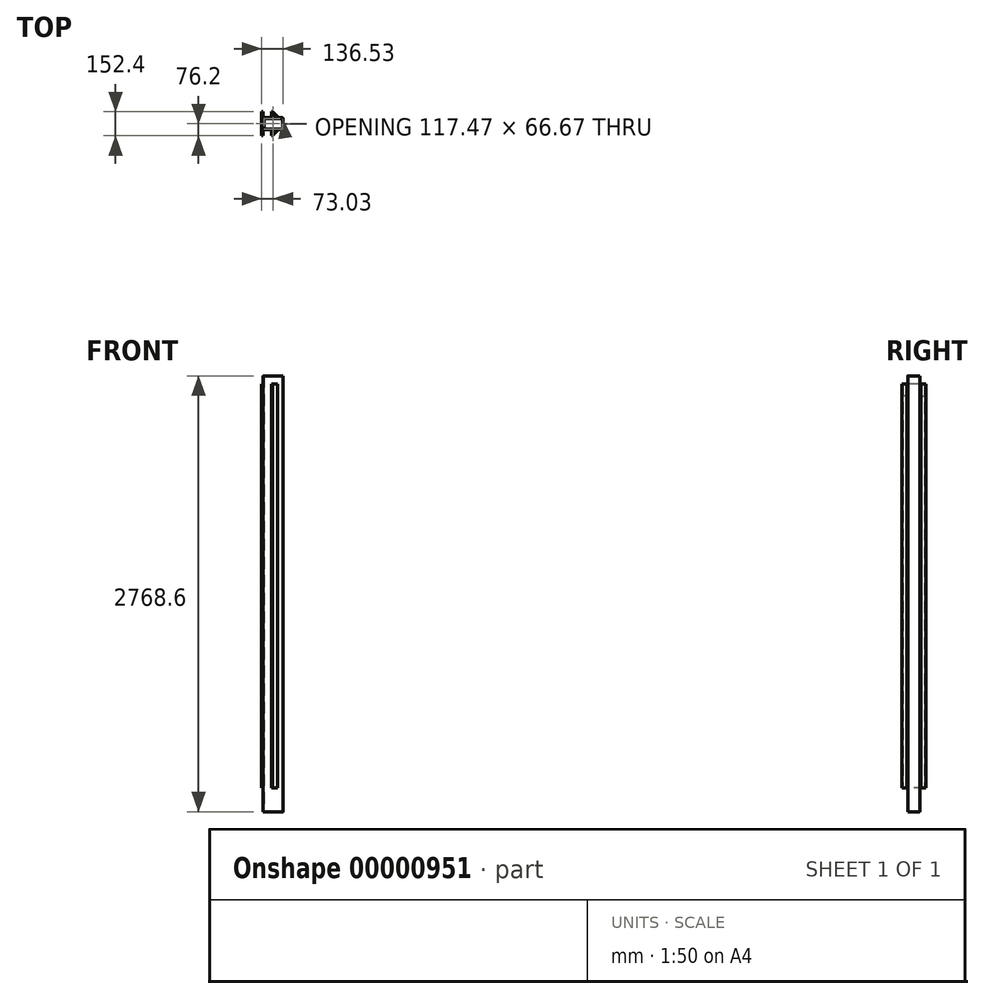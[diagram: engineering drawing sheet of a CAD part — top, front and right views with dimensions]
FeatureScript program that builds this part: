
annotation { "Feature Type Name" : "Feature", "Feature Type Description" : "" }
export const myFeature = defineFeature(function(context is Context, id is Id, definition is map)
    precondition{}
    {
        {
            var Q0;
            Q0=qCreatedBy(makeId("Top.planeOp"),FACE);
            var sketch = newSketch(context, id + "F0", { "sketchPlane" : qUnion([Q0])});
            skLineSegment(sketch, "E0.rect.bottom", {"start": v(-57.15, 38.1) * mm, "end": v(57.15, 38.1) * mm});
            skLineSegment(sketch, "E0.rect.top", {"start": v(-57.15, -38.1) * mm, "end": v(57.15, -38.1) * mm});
            skLineSegment(sketch, "E0.rect.left", {"start": v(-63.5, 31.75) * mm, "end": v(-63.5, -31.75) * mm});
            skLineSegment(sketch, "E0.rect.right", {"start": v(63.5, 31.75) * mm, "end": v(63.5, -31.75) * mm});
            skPoint(sketch, "E0.rect.middle", {"position": v(0, 0) * mm});
            skPoint(sketch, "E1.visualSharp", {"position": v(63.5, -38.1) * mm});
            skArc(sketch, "E1.filletArc", {"start": v(57.15, -38.1) * mm, "mid": v(61.64, -36.24) * mm, "end": v(63.5, -31.75) * mm});
            skPoint(sketch, "E2.visualSharp", {"position": v(63.5, 38.1) * mm});
            skArc(sketch, "E2.filletArc", {"start": v(63.5, 31.75) * mm, "mid": v(61.64, 36.24) * mm, "end": v(57.15, 38.1) * mm});
            skPoint(sketch, "E3.visualSharp", {"position": v(-63.5, -38.1) * mm});
            skArc(sketch, "E3.filletArc", {"start": v(-63.5, -31.75) * mm, "mid": v(-61.64, -36.24) * mm, "end": v(-57.15, -38.1) * mm});
            skPoint(sketch, "E4.visualSharp", {"position": v(-63.5, 38.1) * mm});
            skArc(sketch, "E4.filletArc", {"start": v(-57.15, 38.1) * mm, "mid": v(-61.64, 36.24) * mm, "end": v(-63.5, 31.75) * mm});
            skArc(sketch, "E5.0", {"start": v(58.74, 31.75) * mm, "mid": v(58.27, 32.87) * mm, "end": v(57.15, 33.34) * mm});
            skLineSegment(sketch, "E5.1", {"start": v(-57.15, 33.34) * mm, "end": v(57.15, 33.34) * mm});
            skArc(sketch, "E5.2", {"start": v(-57.15, 33.34) * mm, "mid": v(-58.27, 32.87) * mm, "end": v(-58.74, 31.75) * mm});
            skLineSegment(sketch, "E5.3", {"start": v(-58.74, 31.75) * mm, "end": v(-58.74, -31.75) * mm});
            skArc(sketch, "E5.4", {"start": v(-58.74, -31.75) * mm, "mid": v(-58.27, -32.87) * mm, "end": v(-57.15, -33.34) * mm});
            skLineSegment(sketch, "E5.5", {"start": v(58.74, 31.75) * mm, "end": v(58.74, -31.75) * mm});
            skLineSegment(sketch, "E5.6", {"start": v(-57.15, -33.34) * mm, "end": v(57.15, -33.34) * mm});
            skArc(sketch, "E5.7", {"start": v(57.15, -33.34) * mm, "mid": v(58.27, -32.87) * mm, "end": v(58.74, -31.75) * mm});
            skSolve(sketch);
        }
        {
            var Q0;
            Q0=makeQuery(id+"F0.imprint","IMPRINT",FACE,{"disambiguationData":[TD([[makeQuery(id+"F0.imprint","IMPRINT",EDGE,{"derivedFrom":sQuery(id+"F0.wireOp",EDGE,"E0.rect.bottom")}),-1.0]])]});
            extrude(context, id + "F1", {"entities" : qUnion([Q0]), "depth" : 2768.6 * mm});
        }
        {
            var Q0;
            Q0=makeQuery(id+"F1.opExtrude","SWEPT_FACE",FACE,{"disambiguationData":[OSD([sQuery(id+"F0.wireOp",EDGE,"E0.rect.left")])]});
            var sketch = newSketch(context, id + "F2", { "sketchPlane" : qUnion([Q0])});
            skLineSegment(sketch, "E6", {"start": v(0, 0) * mm, "end": v(0, 354.59) * mm, "construction": true});
            skLineSegment(sketch, "E7.rect.top", {"start": v(-76.2, 152.4) * mm, "end": v(76.2, 152.4) * mm});
            skLineSegment(sketch, "E7.rect.left", {"start": v(-76.2, 2641.6) * mm, "end": v(-76.2, 152.4) * mm});
            skLineSegment(sketch, "E7.rect.right", {"start": v(76.2, 2641.6) * mm, "end": v(76.2, 152.4) * mm});
            skPoint(sketch, "E7.rect.middle", {"position": v(0, 1435.1) * mm});
            skLineSegment(sketch, "E8", {"start": v(-38.1, 2641.6) * mm, "end": v(-76.2, 2641.6) * mm});
            skPoint(sketch, "E9.orphan", {"position": v(-76.2, 2717.8) * mm});
            skLineSegment(sketch, "E10", {"start": v(-38.1, 2641.6) * mm, "end": v(-38.1, 2717.8) * mm});
            skLineSegment(sketch, "E11", {"start": v(-38.1, 2717.8) * mm, "end": v(38.1, 2717.8) * mm});
            skLineSegment(sketch, "E12", {"start": v(38.1, 2717.8) * mm, "end": v(38.1, 2641.6) * mm});
            skLineSegment(sketch, "E13", {"start": v(38.1, 2641.6) * mm, "end": v(76.2, 2641.6) * mm});
            skPoint(sketch, "E14.orphan", {"position": v(76.2, 2717.8) * mm});
            skSolve(sketch);
        }
        {
            var Q0;
            {var subQ4=sQuery(id+"F2.wireOp",EDGE,"E7.rect.right");Q0=makeQuery(id+"F2.imprint","IMPRINT",FACE,{"disambiguationData":[TD([[makeQuery(id+"F2.imprint","IMPRINT",EDGE,{"derivedFrom":subQ4}),-1.0]])]});}
            var Q1;
            {var subQ0=sQuery(id+"F0.wireOp",EDGE,"E0.rect.left");var subQ4=sQuery(id+"F2.wireOp",EDGE,"E7.rect.bottom");var subQ6=makeQuery(id+"F1.opExtrude","SWEPT_EDGE",EDGE,{"disambiguationData":[OSD([subQ0,sQuery(id+"F0.wireOp",EDGE,"E4.filletArc")])]});var subQ8=makeQuery(id+"F2.imprint","INTERSECT",VERTEX,{"derivedFrom":[subQ6,subQ4]});Q1=makeQuery(id+"F2.imprint","IMPRINT",FACE,{"disambiguationData":[TD([[makeQuery(id+"F2.imprint","IMPRINT",EDGE,{"disambiguationData":[TD([[subQ8,-1.0]])],"derivedFrom":subQ4}),-1.0]])]});}
            var Q2;
            {var subQ6=sQuery(id+"F2.wireOp",EDGE,"E7.rect.left");Q2=makeQuery(id+"F2.imprint","IMPRINT",FACE,{"disambiguationData":[TD([[makeQuery(id+"F2.imprint","IMPRINT",EDGE,{"derivedFrom":subQ6}),1.0]])]});}
            var Q3;
            {var subQ0=sQuery(id+"F0.wireOp",EDGE,"E0.rect.left");var subQ4=sQuery(id+"F2.wireOp",EDGE,"E7.rect.top");var subQ6=makeQuery(id+"F1.opExtrude","SWEPT_EDGE",EDGE,{"disambiguationData":[OSD([subQ0,sQuery(id+"F0.wireOp",EDGE,"E4.filletArc")])]});var subQ8=makeQuery(id+"F2.imprint","INTERSECT",VERTEX,{"derivedFrom":[subQ6,subQ4]});Q3=makeQuery(id+"F2.imprint","IMPRINT",FACE,{"disambiguationData":[TD([[makeQuery(id+"F2.imprint","IMPRINT",EDGE,{"disambiguationData":[TD([[subQ8,-1.0]])],"derivedFrom":subQ4}),1.0]])]});}
            extrude(context, id + "F3", {"entities" : qUnion([Q0, Q1, Q2, Q3]), "depth" : 9.52 * mm});
        }
        {
            var Q0;
            Q0=makeQuery(id+"F3.opExtrude","SWEPT_FACE",FACE,{"disambiguationData":[OSD([sQuery(id+"F2.wireOp",EDGE,"E7.rect.top")])]});
            var sketch = newSketch(context, id + "F4", { "sketchPlane" : qUnion([Q0])});
            skLineSegment(sketch, "E15", {"start": v(-9.52, 76.2) * mm, "end": v(-9.52, 38.1) * mm});
            skLineSegment(sketch, "E16", {"start": v(-9.52, 38.1) * mm, "end": v(28.58, 38.1) * mm});
            skLineSegment(sketch, "E17.0", {"start": v(-3.17, 44.45) * mm, "end": v(28.58, 44.45) * mm});
            skLineSegment(sketch, "E17.1", {"start": v(-3.17, 76.2) * mm, "end": v(-3.17, 44.45) * mm});
            skLineSegment(sketch, "E18", {"start": v(-9.52, 76.2) * mm, "end": v(-3.17, 76.2) * mm});
            skLineSegment(sketch, "E19", {"start": v(28.58, 44.45) * mm, "end": v(28.58, 38.1) * mm});
            skSolve(sketch);
        }
        {
            var Q0;
            Q0=makeQuery(id+"F4.imprint","IMPRINT",FACE,{"disambiguationData":[TD([[makeQuery(id+"F4.imprint","IMPRINT",EDGE,{"derivedFrom":sQuery(id+"F4.wireOp",EDGE,"E15")}),1.0]])]});
            extrude(context, id + "F5", {"entities" : qUnion([Q0]), "oppositeDirection" : true, "depth" : 2565.4 * mm});
        }
        {
            var Q0;
            Q0=makeQuery(id+"F5.opExtrude","SWEPT_BODY",BODY,{"disambiguationData":[OSD([sQuery(id+"F4.wireOp",EDGE,"E15"),sQuery(id+"F4.wireOp",EDGE,"E16"),sQuery(id+"F4.wireOp",EDGE,"E17.0"),sQuery(id+"F4.wireOp",EDGE,"E17.1"),sQuery(id+"F4.wireOp",EDGE,"E18"),sQuery(id+"F4.wireOp",EDGE,"E19")])]});
            var Q1;
            Q1=qCreatedBy(makeId("Front.planeOp"),FACE);
            mirror(context, id + "F6", {"entities" : qUnion([Q0]), "mirrorPlane" : qUnion([Q1])});
        }
        {
            var Q0;
            Q0=makeQuery(id+"F5.opExtrude","CAP_FACE",FACE,{"disambiguationData":[OSD([sQuery(id+"F4.wireOp",EDGE,"E15"),sQuery(id+"F4.wireOp",EDGE,"E16"),sQuery(id+"F4.wireOp",EDGE,"E17.0"),sQuery(id+"F4.wireOp",EDGE,"E17.1"),sQuery(id+"F4.wireOp",EDGE,"E18"),sQuery(id+"F4.wireOp",EDGE,"E19")])],"isStart":true});
            var sketch = newSketch(context, id + "F7", { "sketchPlane" : qUnion([Q0])});
            skLineSegment(sketch, "E20", {"start": v(-3.17, 76.2) * mm, "end": v(28.58, 44.45) * mm});
            skLineSegment(sketch, "E21.0", {"start": v(-3.17, 69.46) * mm, "end": v(21.84, 44.45) * mm});
            skLineSegment(sketch, "E22", {"start": v(-3.17, 76.2) * mm, "end": v(-3.17, 69.46) * mm});
            skLineSegment(sketch, "E23", {"start": v(21.84, 44.45) * mm, "end": v(28.58, 44.45) * mm});
            skSolve(sketch);
        }
        {
            var Q0;
            Q0=makeQuery(id+"F7.imprint","IMPRINT",FACE,{"disambiguationData":[TD([[makeQuery(id+"F7.imprint","IMPRINT",EDGE,{"derivedFrom":sQuery(id+"F7.wireOp",EDGE,"E20")}),-1.0]])]});
            extrude(context, id + "F8", {"entities" : qUnion([Q0]), "oppositeDirection" : true, "depth" : 2565.4 * mm});
        }
        {
            var Q0;
            Q0=makeQuery(id+"F8.opExtrude","SWEPT_BODY",BODY,{"disambiguationData":[OSD([sQuery(id+"F7.wireOp",EDGE,"E20"),sQuery(id+"F7.wireOp",EDGE,"E21.0"),sQuery(id+"F7.wireOp",EDGE,"E22"),sQuery(id+"F7.wireOp",EDGE,"E23")])]});
            var Q1;
            Q1=qCreatedBy(makeId("Front.planeOp"),FACE);
            mirror(context, id + "F9", {"entities" : qUnion([Q0]), "mirrorPlane" : qUnion([Q1])});
        }
    });
